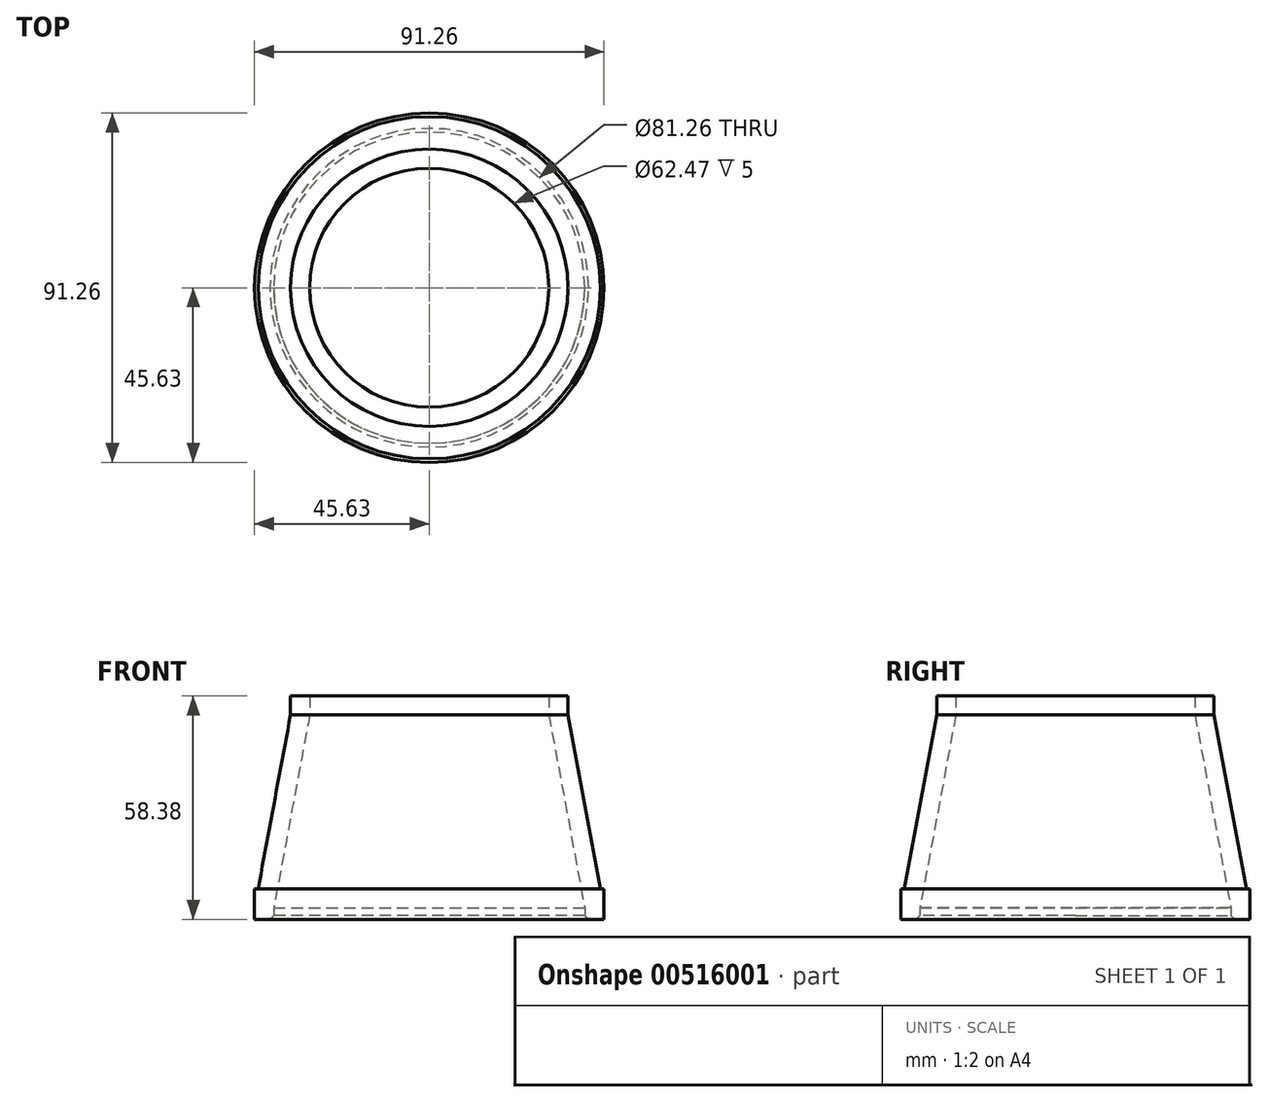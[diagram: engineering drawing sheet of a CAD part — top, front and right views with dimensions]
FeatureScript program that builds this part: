
annotation { "Feature Type Name" : "Feature", "Feature Type Description" : "" }
export const myFeature = defineFeature(function(context is Context, id is Id, definition is map)
    precondition{}
    {
        {
            var Q0;
            Q0=qCreatedBy(makeId("Top.planeOp"),FACE);
            var sketch = newSketch(context, id + "F0", { "sketchPlane" : qUnion([Q0])});
            skCircle(sketch, "E0", {"center": v(0, 0) * mm, "radius": 40.63 * mm});
            skCircle(sketch, "E1", {"center": v(0, 0) * mm, "radius": 45.63 * mm});
            skSolve(sketch);
        }
        {
            var Q0;
            Q0=makeQuery(id+"F0.imprint","IMPRINT",FACE,{"disambiguationData":[TD([[makeQuery(id+"F0.imprint","IMPRINT",EDGE,{"derivedFrom":sQuery(id+"F0.wireOp",EDGE,"E0")}),-1.0]])]});
            extrude(context, id + "F1", {"entities" : qUnion([Q0]), "depth" : 8 * mm, "offsetDistance" : 25.4 * mm});
        }
        {
            var Q0;
            Q0=qCreatedBy(makeId("Right.planeOp"),FACE);
            var sketch = newSketch(context, id + "F2", { "sketchPlane" : qUnion([Q0])});
            skLineSegment(sketch, "E2", {"start": v(0, 16.38) * mm, "end": v(0, 53.38) * mm, "construction": true});
            skLineSegment(sketch, "E3", {"start": v(0, 53.38) * mm, "end": v(31.23, 53.38) * mm, "construction": true});
            skLineSegment(sketch, "E4.0", {"start": v(-45.63, 0) * mm, "end": v(45.63, 0) * mm});
            skLineSegment(sketch, "E5", {"start": v(45.63, 3) * mm, "end": v(36.23, 53.38) * mm});
            skLineSegment(sketch, "E6.0", {"start": v(-40.63, 0) * mm, "end": v(40.63, 0) * mm});
            skLineSegment(sketch, "E7", {"start": v(40.63, 3) * mm, "end": v(31.23, 53.38) * mm});
            skLineSegment(sketch, "E8", {"start": v(45.63, 3) * mm, "end": v(40.63, 3) * mm});
            skLineSegment(sketch, "E9.top", {"start": v(36.23, 58.38) * mm, "end": v(31.23, 58.38) * mm});
            skLineSegment(sketch, "E9.left", {"start": v(36.23, 53.38) * mm, "end": v(36.23, 58.38) * mm});
            skLineSegment(sketch, "E9.right", {"start": v(31.23, 53.38) * mm, "end": v(31.23, 58.38) * mm});
            skSolve(sketch);
        }
        {
            var Q0;
            Q0=makeQuery(id+"F2.imprint","IMPRINT",FACE,{"disambiguationData":[TD([[makeQuery(id+"F2.imprint","IMPRINT",EDGE,{"derivedFrom":sQuery(id+"F2.wireOp",EDGE,"E5")}),1.0]])]});
            var Q1;
            Q1=sQuery(id+"F2.wireOp",EDGE,"E2");
            revolve(context, id + "F3", {"operationType" : NewBodyOperationType.ADD, "entities" : qUnion([Q0]), "axis" : qUnion([Q1]), "revolveType" : RevolveType.FULL});
        }
        {
            var Q0;
            Q0=makeQuery(id+"F1.opExtrude","CAP_EDGE",EDGE,{"disambiguationData":[OSD([sQuery(id+"F0.wireOp",EDGE,"E0")])],"isStart":true});
            chamfer(context, id + "F4", {"entities" : qUnion([Q0]), "width" : 1 * mm, "tangentPropagation" : true});
        }
    });
